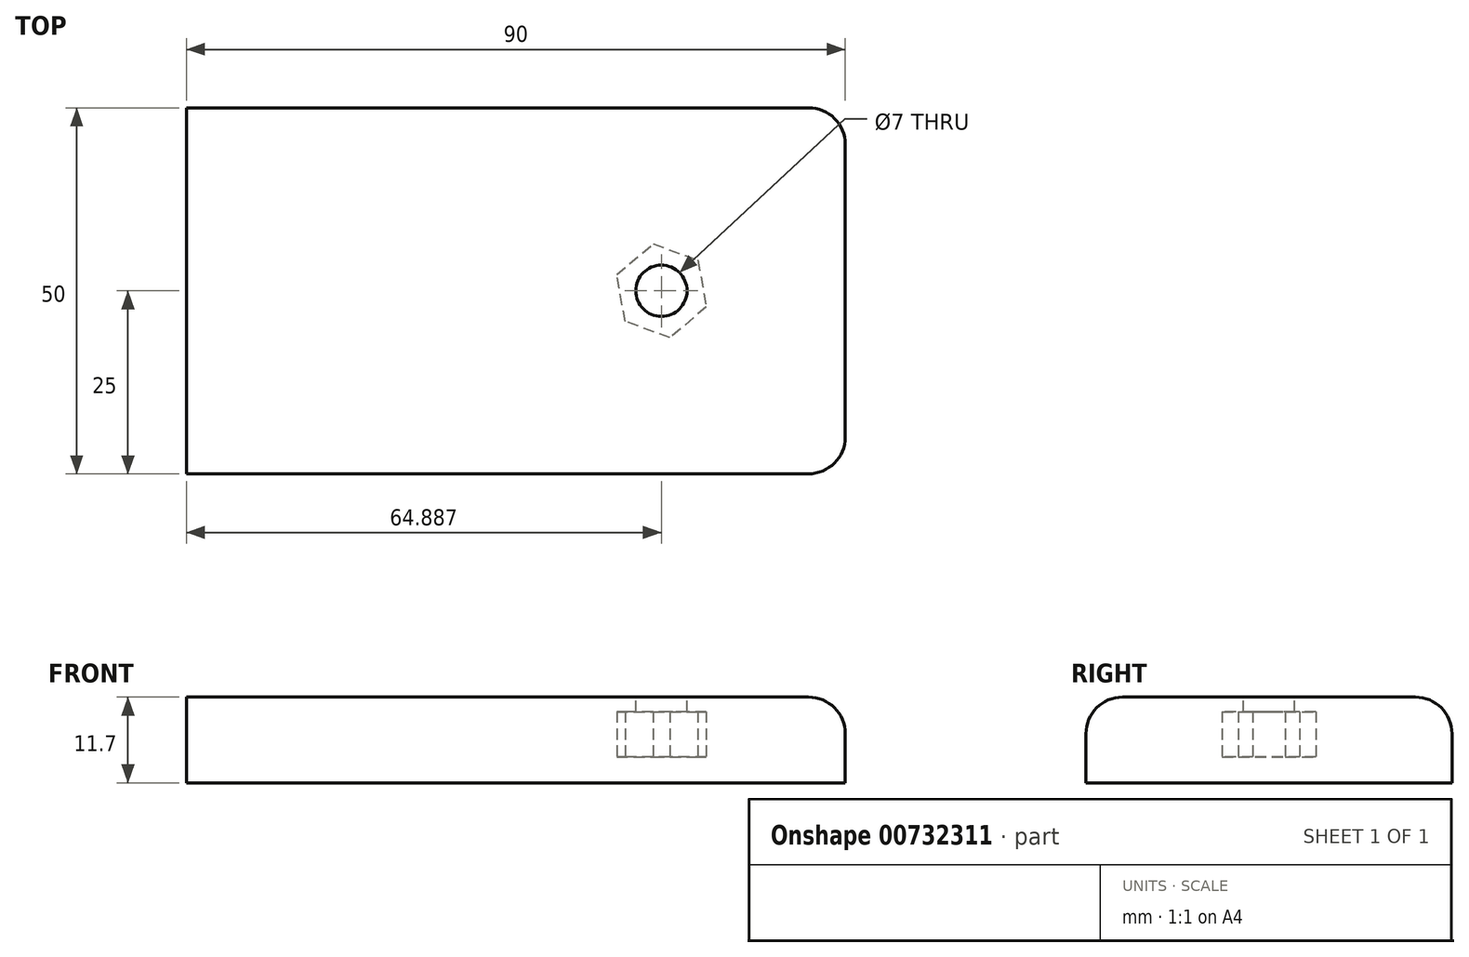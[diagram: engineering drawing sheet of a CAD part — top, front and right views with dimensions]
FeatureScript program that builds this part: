
annotation { "Feature Type Name" : "Feature", "Feature Type Description" : "" }
export const myFeature = defineFeature(function(context is Context, id is Id, definition is map)
    precondition{}
    {
        {
            var Q0;
            Q0=qCreatedBy(makeId("Top.planeOp"),FACE);
            var sketch = newSketch(context, id + "F0", { "sketchPlane" : qUnion([Q0])});
            skLineSegment(sketch, "E0.bottom", {"start": v(45, 25) * mm, "end": v(-45, 25) * mm});
            skLineSegment(sketch, "E0.top", {"start": v(45, -25) * mm, "end": v(-45, -25) * mm});
            skLineSegment(sketch, "E0.left", {"start": v(45, 25) * mm, "end": v(45, -25) * mm});
            skLineSegment(sketch, "E0.right", {"start": v(-45, 25) * mm, "end": v(-45, -25) * mm});
            skPoint(sketch, "E0.middle", {"position": v(0, 0) * mm});
            skSolve(sketch);
        }
        {
            var Q0;
            Q0=makeQuery(id+"F0.imprint","IMPRINT",FACE,{"disambiguationData":[TD([[makeQuery(id+"F0.imprint","IMPRINT",EDGE,{"derivedFrom":sQuery(id+"F0.wireOp",EDGE,"E0.bottom")}),1.0]])]});
            extrude(context, id + "F1", {"entities" : qUnion([Q0]), "depth" : 11.7 * mm, "offsetDistance" : 25 * mm});
        }
        {
            var Q0;
            Q0=makeQuery(id+"F1.opExtrude","CAP_FACE",FACE,{"disambiguationData":[OSD([sQuery(id+"F0.wireOp",EDGE,"E0.bottom"),sQuery(id+"F0.wireOp",EDGE,"E0.top"),sQuery(id+"F0.wireOp",EDGE,"E0.left"),sQuery(id+"F0.wireOp",EDGE,"E0.right")])],"isStart":false});
            var sketch = newSketch(context, id + "F2", { "sketchPlane" : qUnion([Q0])});
            skPoint(sketch, "E1", {"position": v(20, 0) * mm});
            skSolve(sketch);
        }
        {
            var Q0;
            Q0=makeQuery(id+"F2.imprint","IMPRINT",FACE,{"disambiguationData":[TD([[makeQuery(id+"F2.imprint","IMPRINT",EDGE,{"derivedFrom":makeQuery(id+"F1.opExtrude","CAP_EDGE",EDGE,{"disambiguationData":[OSD([sQuery(id+"F0.wireOp",EDGE,"E0.bottom")])],"isStart":false})}),1.0]])]});
            var sketch = newSketch(context, id + "F3", { "sketchPlane" : qUnion([Q0])});
            skCircle(sketch, "E2", {"center": v(19.89, 0) * mm, "radius": 3.5 * mm});
            skSolve(sketch);
        }
        {
            var Q0;
            Q0 = qSketchRegion(id + "F3", true);
            extrude(context, id + "F4", {"entities" : qUnion([Q0]), "operationType" : NewBodyOperationType.REMOVE, "oppositeDirection" : true, "depth" : 8.2 * mm, "offsetDistance" : 25 * mm});
        }
        {
            var Q0;
            Q0=qCreatedBy(makeId("Top.planeOp"),FACE);
            cPlane(context, id + "F5", {"entities" : qUnion([Q0]), "cplaneType" : CPlaneType.OFFSET, "offset" : 3.5 * mm, "width" : 150 * mm, "height" : 150 * mm});
        }
        {
            var Q0;
            Q0=qCreatedBy(id+"F5.planeOp",FACE);
            var sketch = newSketch(context, id + "F6", { "sketchPlane" : qUnion([Q0])});
            skCircle(sketch, "E3.cCircle", {"center": v(19.9, 0) * mm, "radius": 5.63 * mm, "construction": true});
            skLineSegment(sketch, "E3.0", {"start": v(18.76, 6.4) * mm, "end": v(24.88, 4.2) * mm});
            skLineSegment(sketch, "E3.1", {"start": v(24.88, 4.2) * mm, "end": v(26.02, -2.2) * mm});
            skLineSegment(sketch, "E3.2", {"start": v(26.02, -2.2) * mm, "end": v(21.05, -6.4) * mm});
            skLineSegment(sketch, "E3.3", {"start": v(21.05, -6.4) * mm, "end": v(14.94, -4.2) * mm});
            skLineSegment(sketch, "E3.4", {"start": v(14.94, -4.2) * mm, "end": v(13.8, 2.2) * mm});
            skLineSegment(sketch, "E3.5", {"start": v(13.8, 2.2) * mm, "end": v(18.76, 6.4) * mm});
            skPoint(sketch, "E3.0.midPoint", {"position": v(21.82, 5.3) * mm});
            skSolve(sketch);
        }
        {
            var Q0;
            Q0 = qSketchRegion(id + "F6", true);
            extrude(context, id + "F7", {"entities" : qUnion([Q0]), "operationType" : NewBodyOperationType.REMOVE, "depth" : 6.2 * mm, "offsetDistance" : 25 * mm});
        }
        {
            var Q0;
            Q0=makeQuery(id+"F1.opExtrude","CAP_EDGE",EDGE,{"disambiguationData":[OSD([sQuery(id+"F0.wireOp",EDGE,"E0.top")])],"isStart":false});
            var Q1;
            Q1=makeQuery(id+"F1.opExtrude","CAP_EDGE",EDGE,{"disambiguationData":[OSD([sQuery(id+"F0.wireOp",EDGE,"E0.left")])],"isStart":false});
            var Q2;
            Q2=makeQuery(id+"F1.opExtrude","CAP_EDGE",EDGE,{"disambiguationData":[OSD([sQuery(id+"F0.wireOp",EDGE,"E0.bottom")])],"isStart":false});
            var Q3;
            Q3=makeQuery(id+"F1.opExtrude","SWEPT_EDGE",EDGE,{"disambiguationData":[OSD([sQuery(id+"F0.wireOp",EDGE,"E0.top"),sQuery(id+"F0.wireOp",EDGE,"E0.left")])]});
            var Q4;
            Q4=makeQuery(id+"F1.opExtrude","SWEPT_EDGE",EDGE,{"disambiguationData":[OSD([sQuery(id+"F0.wireOp",EDGE,"E0.bottom"),sQuery(id+"F0.wireOp",EDGE,"E0.left")])]});
            fillet(context, id + "F8", {"entities" : qUnion([Q0, Q1, Q2, Q3, Q4]), "radius" : 5 * mm, "tangentPropagation" : true, "allowEdgeOverflow" : false});
        }
    });
